# Revit family: 90002105 - Aventa Silent AVS 250 - BIM file
name_source: partatom
category: Mechanical Equipment
units: mm (PartAtom-declared; Revit-internal decimal feet)

## family parameters
Always vertical = No
Classification = None
Cut with Voids When Loaded = No
Maintain Annotation Orientation = No
OmniClass Number = 23.75.35.17.11
OmniClass Title = Fans for Air Ductwork
Part Type = Breaks Into
Room Calculation Point = No
Round Connector Dimension = Use Diameter
Shared = No
Work Plane-Based = No

## types (2) — shared parameters
Current = 1 A
D = 250 mm  [stored 0.82021 ft]
D1 = 358 mm  [stored 1.17454 ft]
Dd12 = 1 mm  [stored 0.00328084 ft]
Dd13 = 2 mm  [stored 0.00656168 ft]
Dd14 = 6 mm  [stored 0.019685 ft]
Dd16 = 52 mm
Dd22 = 5 mm  [stored 0.0164042 ft]
Dd23 = 6 mm  [stored 0.019685 ft]
Dd24 = 30 mm  [stored 0.0984252 ft]
Dd26 = 52 mm
Description = Inline mixed-flow fan suitable for domestic and light commercial facilities
Dimensions = (H) 360 x (W) 658 x (D) 445mm
Distribution Box Material = Distribution Box Dark Grey
Duct Connection Size = 250 mm  [stored 0.82021 ft]
ElBoxH = 53 mm  [stored 0.173885 ft]
ElBoxL = 104 mm
ElBoxR = 15 mm  [stored 0.0492126 ft]
ElBoxW = 104 mm
Family Version = 1.0
Fan Material = Metal Black
Hanger Material = Metal Zinc
HangerBaseH = 182 mm  [stored 0.597113 ft]
HangerExtraL = No
HangerH = 182 mm  [stored 0.597113 ft]
HangerL = 402 mm  [stored 1.3189 ft]
HangerL1 = 332 mm  [stored 1.08924 ft]
HangerW = 150 mm  [stored 0.492126 ft]
L = 658 mm  [stored 2.15879 ft]
L1 = 32 mm  [stored 0.104987 ft]
L11 = 176 mm  [stored 0.577428 ft]
L12 = 3 mm  [stored 0.00984252 ft]
L13 = 4 mm  [stored 0.0131234 ft]
L14 = 10 mm  [stored 0.0328084 ft]
L15 = 144 mm  [stored 0.472441 ft]
L16 = 6 mm  [stored 0.019685 ft]
L17 = 9 mm  [stored 0.0295276 ft]
L2 = 32 mm  [stored 0.104987 ft]
L21 = 218 mm  [stored 0.715223 ft]
L22 = 8 mm  [stored 0.0262467 ft]
L23 = 13 mm
L24 = 23 mm  [stored 0.0754593 ft]
L25 = 159 mm
L26 = 6 mm  [stored 0.019685 ft]
L27 = 9 mm  [stored 0.0295276 ft]
Load Classification = HVAC
Maintenance Zone Height = 600 mm  [stored 1.9685 ft]
Maintenance Zone Length = 600 mm  [stored 1.9685 ft]
Maintenance Zone Length Calc = 658 mm  [stored 2.15879 ft]
Maintenance Zone Material = Maintenance Zone
Maintenance Zone Width = 600 mm  [stored 1.9685 ft]
Manufacturer = Airflow
Material finish = Polymer Coated Steel
Number of Poles = 1
Power Factor = 1
Protection rating = IPX4
R1 = 179 mm  [stored 0.58727 ft]
RPM (min-1) = 2440
Transported Air Temperature (°C) = -25...+60
URL = https://www.airflow.com
Voltage = 230 V
Weight = 15.00 kg
zero-valued in all types: Default Elevation

## per-type parameters (varying)
| type | Airflow part no | Apparent Power | Maximum Air Flow | Model | Noise Level at 3 m (dBa) | Power | Type Comments |
| Aventa Silent AVS250 Timer | 90002122 | 177 VA | 1400 m³/h | Aventa Silent AVS250 Timer | 38 | 177 W | Inline fan single speed up to 1400m3/h |
| Aventa Silent AV250 Basic | 90002105 | 125 VA | 1110 m³/h | Aventa Silent AVS250 Basic | 34 | 125 W | Inline fan single speed up to 1110m3/h |

note: [stored X ft] marks values corroborated as IEEE doubles in the binary element streams (Revit-internal decimal feet)

## geometry (parser evidence)
native form markers: Sweep x11
no freeform markers — native parametric forms only
